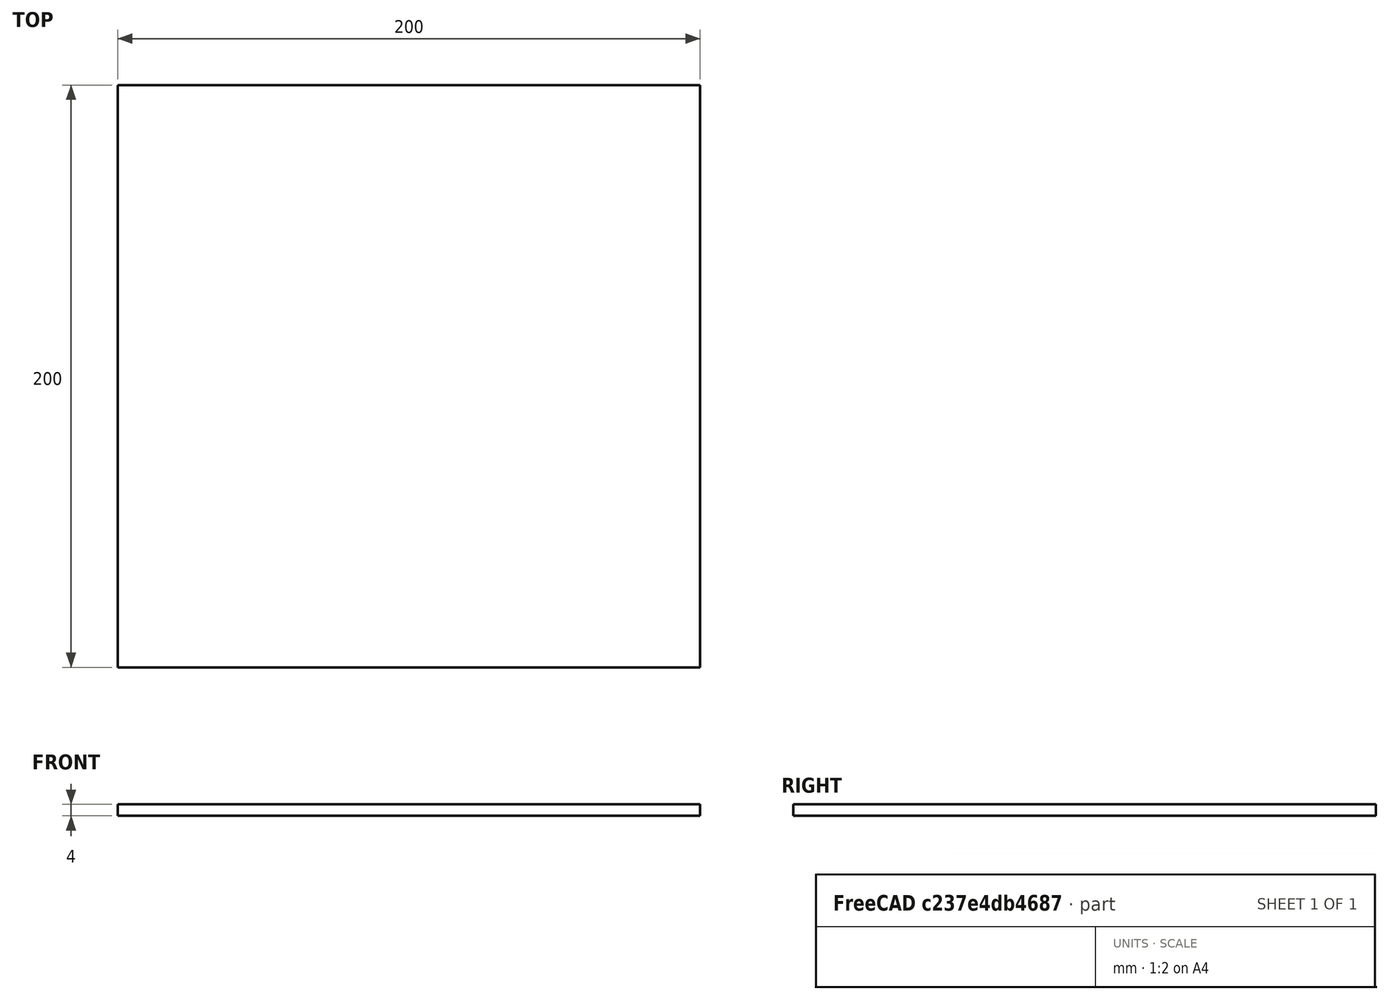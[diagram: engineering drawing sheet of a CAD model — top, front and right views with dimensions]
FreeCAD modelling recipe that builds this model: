
FCSTD DOCUMENT  (FreeCAD 0.18R16131 (Git))
Label: Glass_Box_Metallic_Coating
License: All rights reserved
LicenseURL: http://en.wikipedia.org/wiki/All_rights_reserved
objects: Part::Feature×5, Part::Box×1, Part::Plane×1
note: 7 computed .brp shape members not serialized (recipe doc carries the construction recipe); baked Part::Feature solids carry a one-line shape summary decoded from their .brp

FEATURE [Part::Box] Box_Glass  label="Box_Glass(Glass)"
  AttacherType = Attacher::AttachEngine3D
  Height = 4
  Length = 200
  Placement = pos=(-100,-100,0) rot=(0,0,1;0rad)
  Width = 200
FEATURE [Part::Plane] Trans_Abs  label="Absorber(Trans_Abs)"
  AttacherType = Attacher::AttachEngine3D
  Length = 200
  Placement = pos=(-100,-100,4.001) rot=(0,0,1;0rad)
  Width = 200
FEATURE [Part::Feature] Mirror_1  label="Mirror_1(Mirror)"
  shape: bbox 200 x 2e-07 x 4.001 mm, 1 faces, 0 solids (baked)
FEATURE [Part::Feature] Mirror_2  label="Mirror_2(Mirror)"
  Placement = pos=(0,200,0) rot=(0,0,1;0rad)
  shape: bbox 200 x 2e-07 x 4.001 mm, 1 faces, 0 solids (baked)
FEATURE [Part::Feature] Mirror_3  label="Mirror_3(Mirror)"
  shape: bbox 2e-07 x 200 x 4.001 mm, 1 faces, 0 solids (baked)
FEATURE [Part::Feature] Mirror_4  label="Mirror_4(Mirror)"
  Placement = pos=(-200,0,0) rot=(0,0,1;0rad)
  shape: bbox 2e-07 x 200 x 4.001 mm, 1 faces, 0 solids (baked)
FEATURE [Part::Feature] Face004  label="Coating(Ag)"
  Placement = pos=(-100,-100,0) rot=(0,0,1;0rad)
  shape: bbox 200 x 200 x 2e-07 mm, 1 faces, 0 solids (baked)
